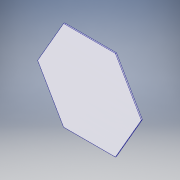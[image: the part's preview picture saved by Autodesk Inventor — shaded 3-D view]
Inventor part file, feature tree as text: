
AUTODESK INVENTOR PART (.ipt)
format: ipt  version: 2019 (Build 230136000, 136)  size: 95,744 bytes
history: native  units: mm
features: extrude x1, sketch x1
ambient origin geometry x8: Origin, YZ Plane, XZ Plane, XY Plane, X Axis, Y Axis, Z Axis, Center Point
bodies: Solid1 (feature_tree)
feature tree (2):
  extrude  "Extrusion1"  Depth=2.0mm TaperAngle=0.0deg
  sketch  "Sketch1"  dims[d0=180.0mm d1=2.0mm d2=0.0mm]
